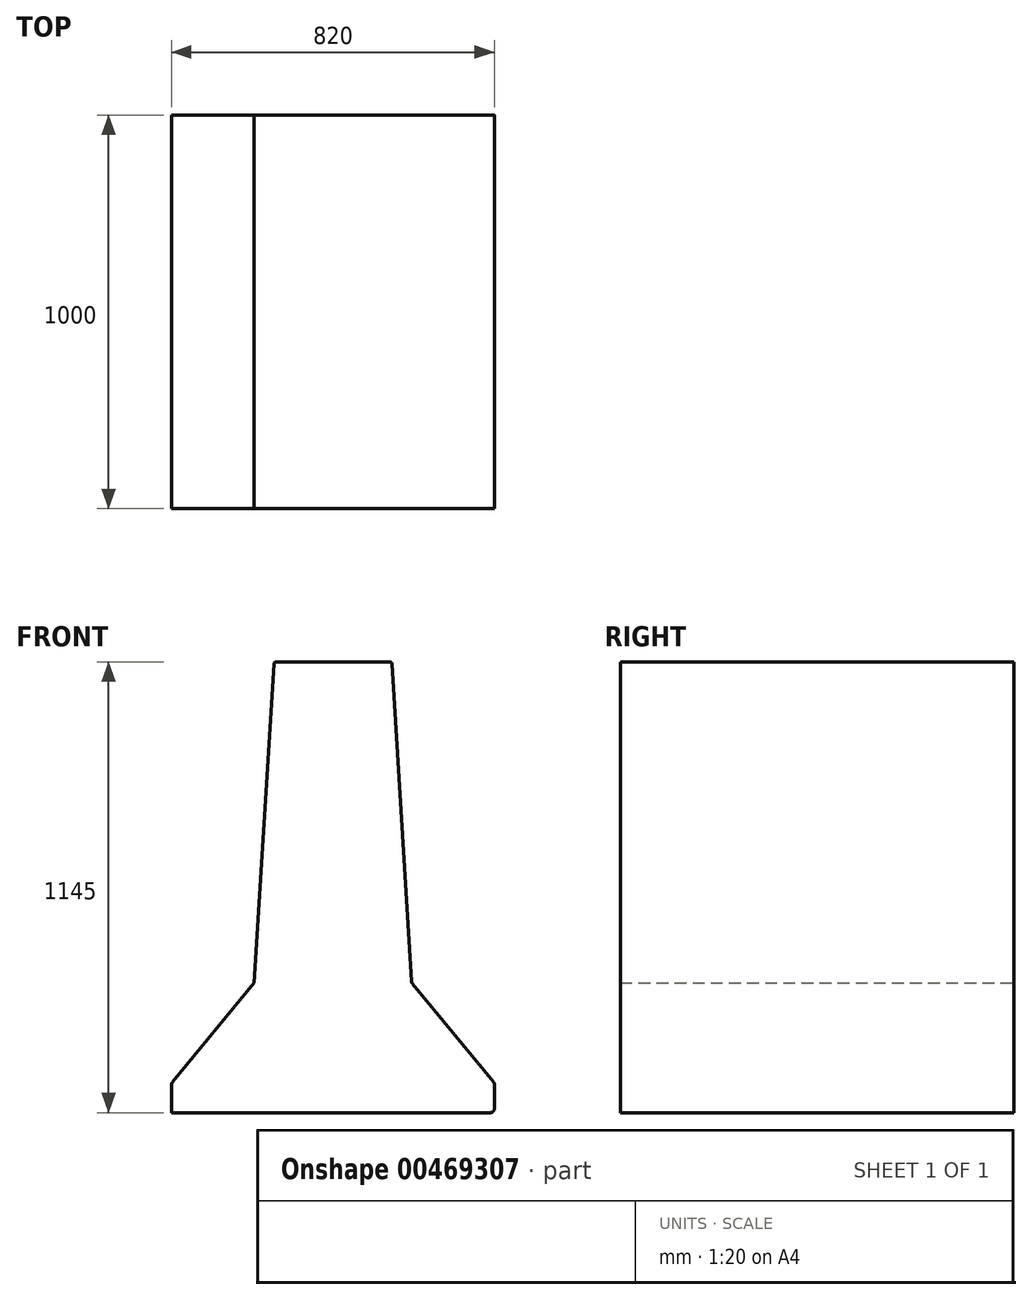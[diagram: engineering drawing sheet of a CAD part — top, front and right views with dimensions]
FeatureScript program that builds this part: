
annotation { "Feature Type Name" : "Feature", "Feature Type Description" : "" }
export const myFeature = defineFeature(function(context is Context, id is Id, definition is map)
    precondition{}
    {
        {
            var Q0;
            Q0=qCreatedBy(makeId("Front.planeOp"),FACE);
            var sketch = newSketch(context, id + "F0", { "sketchPlane" : qUnion([Q0])});
            skLineSegment(sketch, "E0", {"start": v(0, 0) * mm, "end": v(400, 0) * mm});
            skLineSegment(sketch, "E1", {"start": v(410, 10) * mm, "end": v(410, 71.41) * mm});
            skLineSegment(sketch, "E2", {"start": v(407.72, 77.77) * mm, "end": v(202.06, 327.5) * mm});
            skLineSegment(sketch, "E3", {"start": v(199.8, 333.24) * mm, "end": v(150.29, 1140.3) * mm});
            skLineSegment(sketch, "E4", {"start": v(145.3, 1145) * mm, "end": v(0, 1145) * mm});
            skLineSegment(sketch, "E5.MirrorCS", {"start": v(-145.3, 1145) * mm, "end": v(0, 1145) * mm});
            skLineSegment(sketch, "E6.MirrorCS", {"start": v(-410, 0) * mm, "end": v(-410, 71.41) * mm});
            skLineSegment(sketch, "E7.MirrorCS", {"start": v(-407.72, 77.77) * mm, "end": v(-201.03, 328.75) * mm});
            skLineSegment(sketch, "E8", {"start": v(0, 0) * mm, "end": v(-410, 0) * mm});
            skPoint(sketch, "E9.visualSharp", {"position": v(-150, 1145) * mm});
            skArc(sketch, "E9.filletArc", {"start": v(-145.3, 1145) * mm, "mid": v(-148.72, 1143.64) * mm, "end": v(-150.29, 1140.3) * mm});
            skPoint(sketch, "E10.visualSharp", {"position": v(150, 1145) * mm});
            skArc(sketch, "E10.filletArc", {"start": v(150.29, 1140.3) * mm, "mid": v(148.72, 1143.64) * mm, "end": v(145.3, 1145) * mm});
            skPoint(sketch, "E11.visualSharp", {"position": v(-200, 330) * mm});
            skPoint(sketch, "E12.visualSharp", {"position": v(-410, 75) * mm});
            skArc(sketch, "E12.filletArc", {"start": v(-407.72, 77.77) * mm, "mid": v(-409.41, 74.79) * mm, "end": v(-410, 71.41) * mm});
            skLineSegment(sketch, "E13", {"start": v(-200, 330) * mm, "end": v(-201.03, 328.75) * mm});
            skLineSegment(sketch, "E14", {"start": v(-150.29, 1140.3) * mm, "end": v(-200, 330) * mm});
            skPoint(sketch, "E15.visualSharp", {"position": v(200, 330) * mm});
            skArc(sketch, "E15.filletArc", {"start": v(199.8, 333.24) * mm, "mid": v(200.48, 330.19) * mm, "end": v(202.06, 327.5) * mm});
            skPoint(sketch, "E16.visualSharp", {"position": v(410, 75) * mm});
            skArc(sketch, "E16.filletArc", {"start": v(410, 71.41) * mm, "mid": v(409.41, 74.79) * mm, "end": v(407.72, 77.77) * mm});
            skPoint(sketch, "E17.visualSharp", {"position": v(410, 0) * mm});
            skArc(sketch, "E17.filletArc", {"start": v(400, 0) * mm, "mid": v(407.07, 2.93) * mm, "end": v(410, 10) * mm});
            skSolve(sketch);
        }
        {
            var Q0;
            Q0 = qSketchRegion(id + "F0", true);
            extrude(context, id + "F1", {"entities" : qUnion([Q0]), "depth" : 1000 * mm});
        }
    });
